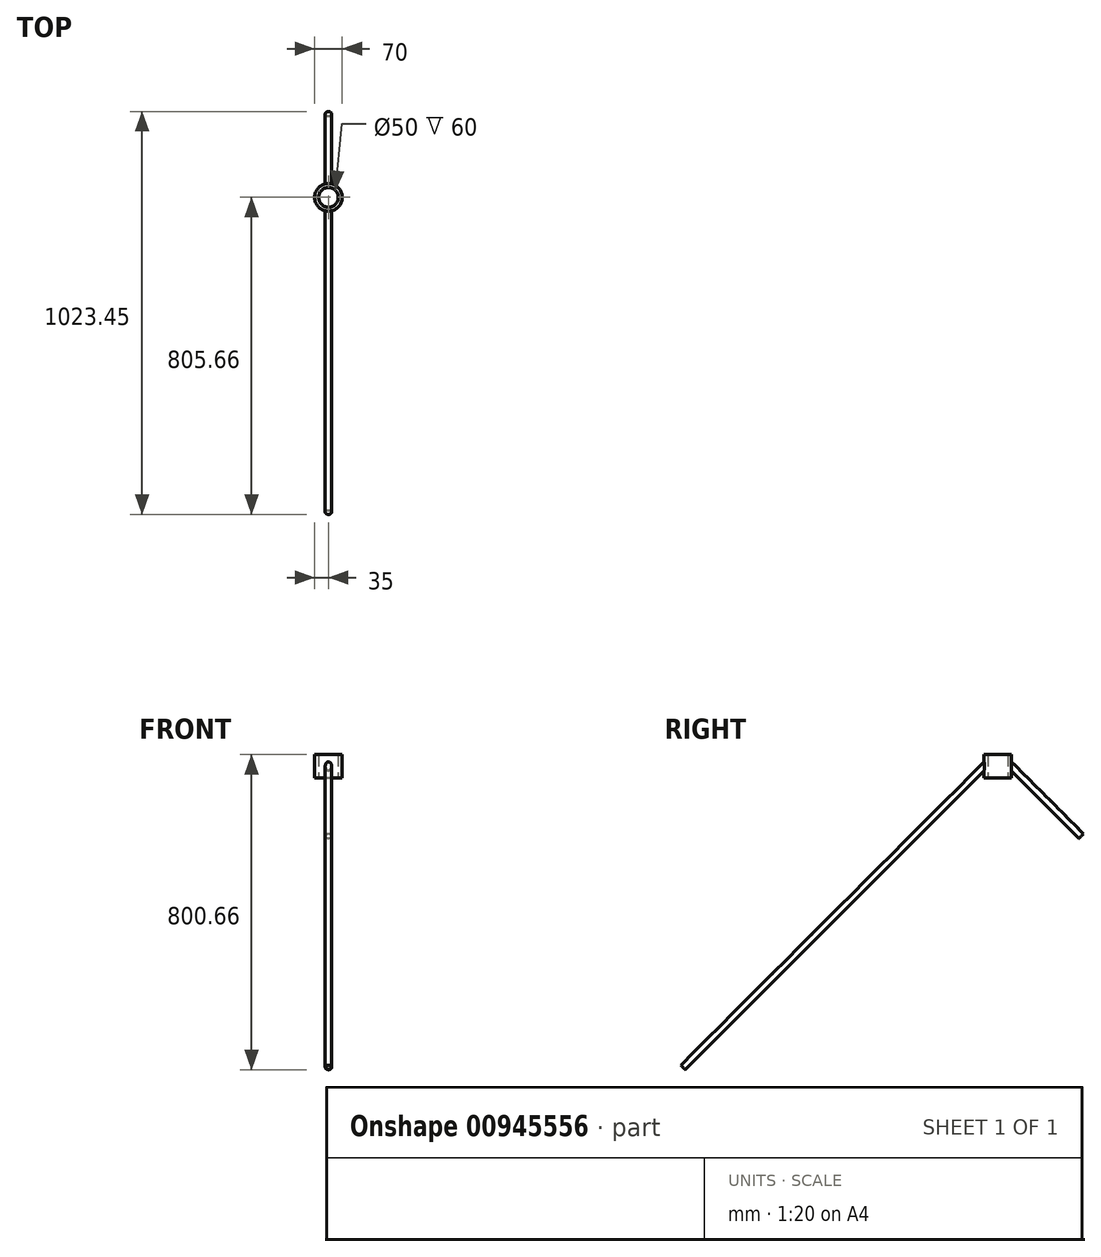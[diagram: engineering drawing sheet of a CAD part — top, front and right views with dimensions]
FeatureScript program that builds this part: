
annotation { "Feature Type Name" : "Feature", "Feature Type Description" : "" }
export const myFeature = defineFeature(function(context is Context, id is Id, definition is map)
    precondition{}
    {
        {
            var Q0;
            Q0=qCreatedBy(makeId("Right.planeOp"),FACE);
            var sketch = newSketch(context, id + "F0", { "sketchPlane" : qUnion([Q0])});
            skLineSegment(sketch, "E0", {"start": v(0, 0) * mm, "end": v(-800, -800) * mm});
            skLineSegment(sketch, "E1", {"start": v(0, 0) * mm, "end": v(212.13, -212.13) * mm});
            skSolve(sketch);
        }
        {
            var Q0;
            Q0=sQuery(id+"F0.wireOp",EDGE,"E0");
            var Q1;
            Q1=sQuery(id+"F0.wireOp",VERTEX,"E0.end");
            cPlane(context, id + "F1", {"entities" : qUnion([Q0, Q1]), "cplaneType" : CPlaneType.LINE_POINT, "offset" : 25 * mm, "width" : 150 * mm, "height" : 150 * mm});
        }
        {
            var Q0;
            Q0=qCreatedBy(id+"F1.planeOp",FACE);
            var sketch = newSketch(context, id + "F2", { "sketchPlane" : qUnion([Q0])});
            skCircle(sketch, "E2", {"center": v(0, 0) * mm, "radius": 8 * mm});
            skCircle(sketch, "E3", {"center": v(0, 0) * mm, "radius": 7 * mm});
            skSolve(sketch);
        }
        {
            var Q0;
            Q0=makeQuery(id+"F2.imprint","IMPRINT",FACE,{"disambiguationData":[TD([[makeQuery(id+"F2.imprint","IMPRINT",EDGE,{"derivedFrom":sQuery(id+"F2.wireOp",EDGE,"E2")}),1.0]])]});
            var Q1;
            Q1=sQuery(id+"F0.wireOp",EDGE,"E0");
            var Q2;
            Q2=sQuery(id+"F0.wireOp",EDGE,"E1");
            sweep(context, id + "F3", {"profiles" : qUnion([Q0]), "path" : qUnion([Q1, Q2])});
        }
        {
            var Q0;
            Q0=qCreatedBy(makeId("Top.planeOp"),FACE);
            var sketch = newSketch(context, id + "F4", { "sketchPlane" : qUnion([Q0])});
            skCircle(sketch, "E4", {"center": v(0, 0) * mm, "radius": 25 * mm});
            skSolve(sketch);
        }
        {
            var Q0;
            Q0 = qSketchRegion(id + "F4", true);
            extrude(context, id + "F5", {"entities" : qUnion([Q0]), "operationType" : NewBodyOperationType.REMOVE, "endBound" : BoundingType.SYMMETRIC, "depth" : 80 * mm, "offsetDistance" : 25 * mm});
        }
        {
            var Q0;
            Q0=qCreatedBy(makeId("Top.planeOp"),FACE);
            var sketch = newSketch(context, id + "F6", { "sketchPlane" : qUnion([Q0])});
            skCircle(sketch, "E5", {"center": v(0, 0) * mm, "radius": 25 * mm});
            skCircle(sketch, "E6", {"center": v(0, 0) * mm, "radius": 35 * mm});
            skSolve(sketch);
        }
        {
            var Q0;
            Q0 = qSketchRegion(id + "F6", true);
            extrude(context, id + "F7", {"entities" : qUnion([Q0]), "operationType" : NewBodyOperationType.ADD, "oppositeDirection" : true, "depth" : 65 * mm, "offsetDistance" : 25 * mm, "hasSecondDirection" : true, "secondDirectionOppositeDirection" : false, "secondDirectionDepth" : -5 * mm});
        }
    });
